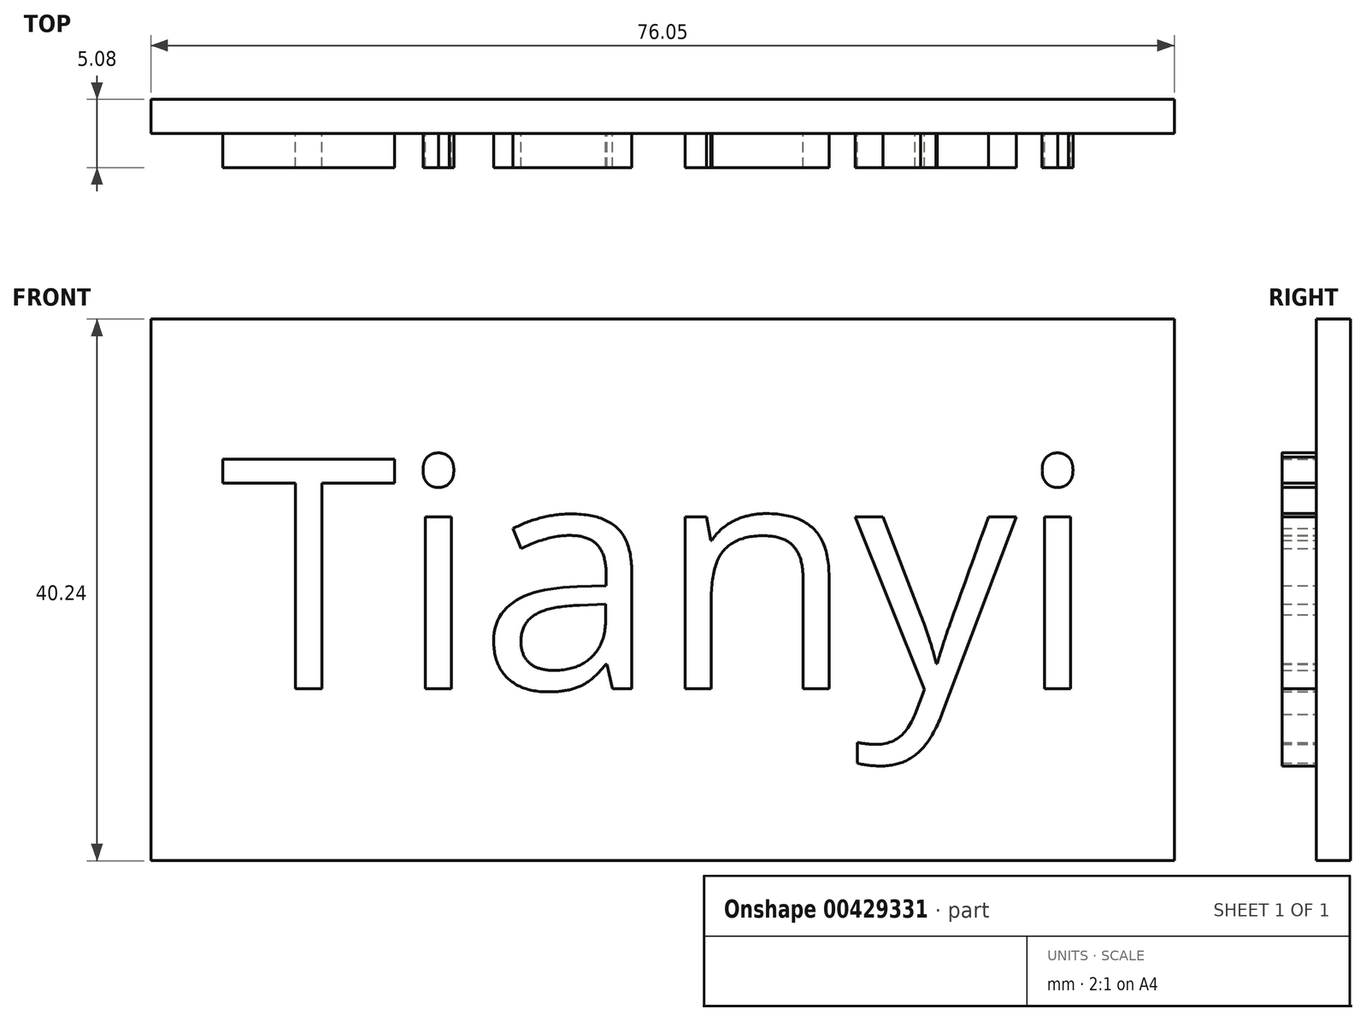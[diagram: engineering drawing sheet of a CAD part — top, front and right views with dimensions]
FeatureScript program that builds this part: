
annotation { "Feature Type Name" : "Feature", "Feature Type Description" : "" }
export const myFeature = defineFeature(function(context is Context, id is Id, definition is map)
    precondition{}
    {
        {
            var Q0;
            Q0=qCreatedBy(makeId("Front.planeOp"),FACE);
            var sketch = newSketch(context, id + "F0", { "sketchPlane" : qUnion([Q0])});
            skLineSegment(sketch, "E0", {"start": v(0, 0) * mm, "end": v(76.05, 0) * mm});
            skLineSegment(sketch, "E1", {"start": v(76.05, 0) * mm, "end": v(76.05, -40.24) * mm});
            skLineSegment(sketch, "E2", {"start": v(0, -40.24) * mm, "end": v(76.05, -40.24) * mm});
            skLineSegment(sketch, "E3", {"start": v(0, 0) * mm, "end": v(0, -40.24) * mm});
            skSolve(sketch);
        }
        {
            var Q0;
            Q0=makeQuery(id+"F0.imprint","IMPRINT",FACE,{"disambiguationData":[TD([[makeQuery(id+"F0.imprint","IMPRINT",EDGE,{"derivedFrom":sQuery(id+"F0.wireOp",EDGE,"E0")}),-1.0]])]});
            var sketch = newSketch(context, id + "F1", { "sketchPlane" : qUnion([Q0])});
            skText(sketch, "E4", { "text": "Tianyi", "fontName": "OpenSans-Regular.ttf"});
            const initialGuessF1  = {"E4": [0.00513, -0.02746, 1, 0, 0.01719]};
            skSetInitialGuess(sketch, initialGuessF1);
            skSolve(sketch);
        }
        {
            var Q0;
            Q0=makeQuery(id+"F0.imprint","IMPRINT",FACE,{"disambiguationData":[TD([[makeQuery(id+"F0.imprint","IMPRINT",EDGE,{"derivedFrom":sQuery(id+"F0.wireOp",EDGE,"E0")}),-1.0]])]});
            extrude(context, id + "F2", {"entities" : qUnion([Q0]), "depth" : 2.54 * mm});
        }
        {
            var Q0;
            Q0=qSketchRegion(id+"F1",true);
            extrude(context, id + "F3", {"entities" : qUnion([Q0]), "operationType" : NewBodyOperationType.ADD, "depth" : 5.08 * mm});
        }
    });
